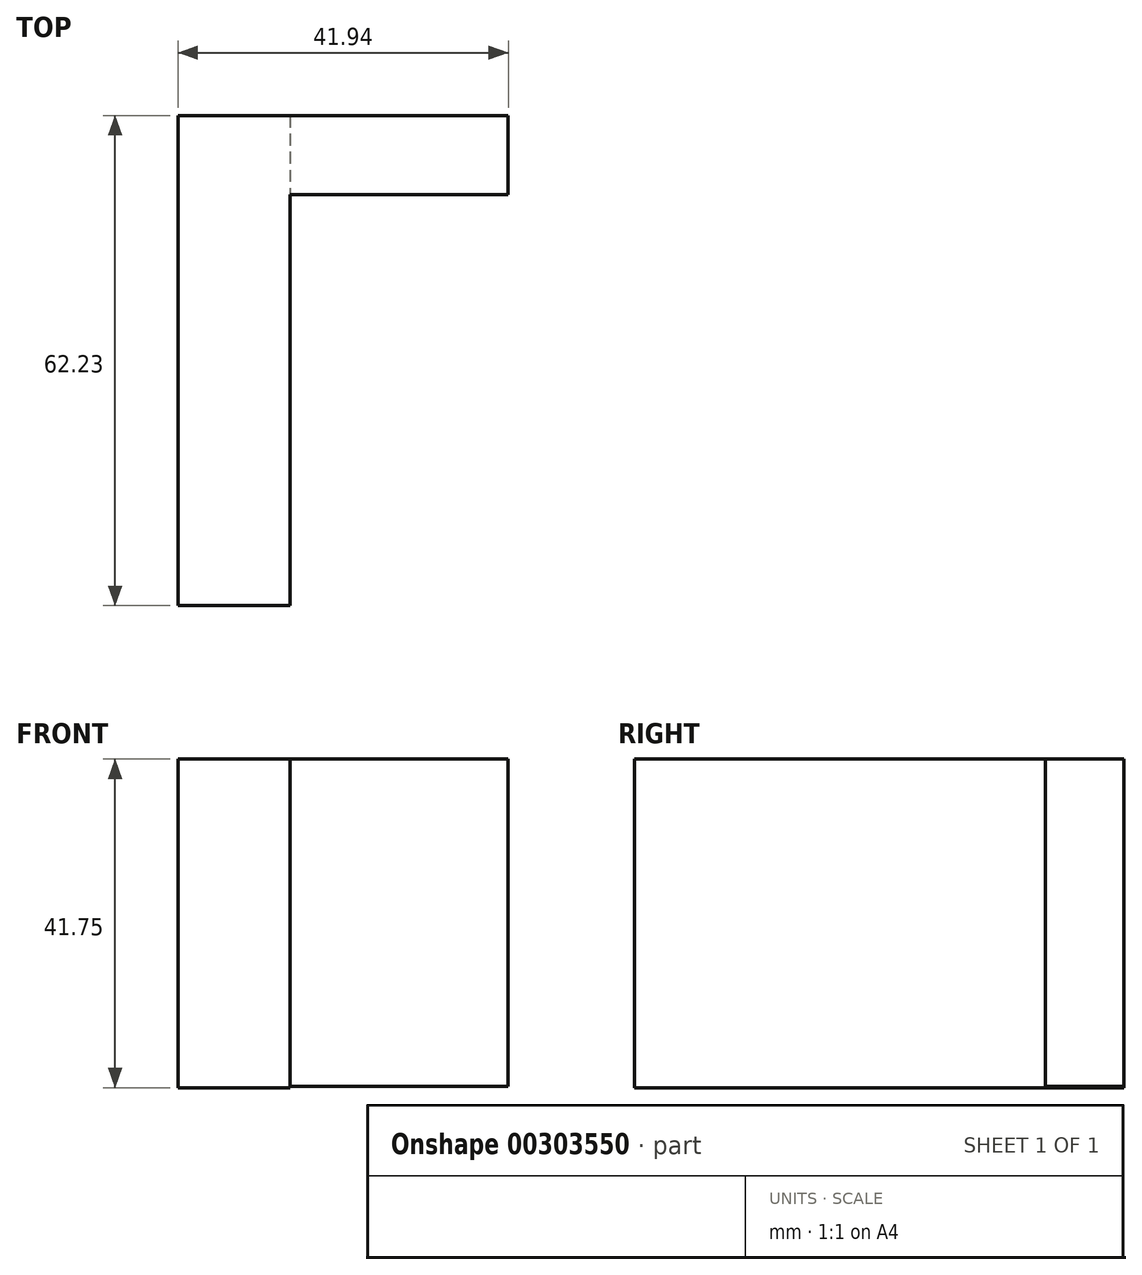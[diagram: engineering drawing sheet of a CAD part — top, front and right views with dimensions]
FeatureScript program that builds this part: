
annotation { "Feature Type Name" : "Feature", "Feature Type Description" : "" }
export const myFeature = defineFeature(function(context is Context, id is Id, definition is map)
    precondition{}
    {
        {
            var Q0;
            Q0=qCreatedBy(makeId("Front.planeOp"),FACE);
            var sketch = newSketch(context, id + "F0", { "sketchPlane" : qUnion([Q0])});
            skLineSegment(sketch, "E0.bottom", {"start": v(-64.74, 48.22) * mm, "end": v(-22.8, 48.22) * mm});
            skLineSegment(sketch, "E0.top", {"start": v(-64.74, 6.67) * mm, "end": v(-22.8, 6.67) * mm});
            skLineSegment(sketch, "E0.left", {"start": v(-64.74, 48.22) * mm, "end": v(-64.74, 6.67) * mm});
            skLineSegment(sketch, "E0.right", {"start": v(-22.8, 48.22) * mm, "end": v(-22.8, 6.67) * mm});
            skSolve(sketch);
        }
        {
            var Q0;
            Q0=makeQuery(id+"F0.imprint","IMPRINT",FACE,{"disambiguationData":[TD([[makeQuery(id+"F0.imprint","IMPRINT",EDGE,{"derivedFrom":sQuery(id+"F0.wireOp",EDGE,"E0.bottom")}),-1.0]])]});
            extrude(context, id + "F1", {"entities" : qUnion([Q0]), "depth" : 10 * mm});
        }
        {
            var Q0;
            Q0=makeQuery(id+"F1.opExtrude","SWEPT_FACE",FACE,{"disambiguationData":[OSD([sQuery(id+"F0.wireOp",EDGE,"E0.left")])]});
            var sketch = newSketch(context, id + "F2", { "sketchPlane" : qUnion([Q0])});
            skLineSegment(sketch, "E1.bottom", {"start": v(0, 48.22) * mm, "end": v(62.23, 48.22) * mm});
            skLineSegment(sketch, "E1.top", {"start": v(0, 6.47) * mm, "end": v(62.23, 6.47) * mm});
            skLineSegment(sketch, "E1.left", {"start": v(0, 48.22) * mm, "end": v(0, 6.47) * mm});
            skLineSegment(sketch, "E1.right", {"start": v(62.23, 48.22) * mm, "end": v(62.23, 6.47) * mm});
            skSolve(sketch);
        }
        {
            var Q0;
            {var subQ3=sQuery(id+"F0.wireOp",EDGE,"E0.left");var subQ4=makeQuery(id+"F1.opExtrude","CAP_EDGE",EDGE,{"disambiguationData":[OSD([subQ3])],"isStart":false});Q0=makeQuery(id+"F2.imprint","IMPRINT",FACE,{"disambiguationData":[TD([[makeQuery(id+"F2.imprint","IMPRINT",EDGE,{"derivedFrom":subQ4}),-1.0]])]});}
            var Q1;
            {var subQ3=sQuery(id+"F2.wireOp",EDGE,"E1.top");Q1=makeQuery(id+"F2.imprint","IMPRINT",FACE,{"disambiguationData":[TD([[makeQuery(id+"F2.imprint","IMPRINT",EDGE,{"derivedFrom":subQ3}),1.0]])]});}
            extrude(context, id + "F3", {"entities" : qUnion([Q0, Q1]), "operationType" : NewBodyOperationType.ADD, "oppositeDirection" : true, "depth" : 14.2 * mm});
        }
    });
